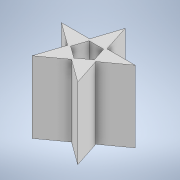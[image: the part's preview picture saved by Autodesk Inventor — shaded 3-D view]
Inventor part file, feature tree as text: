
AUTODESK INVENTOR PART (.ipt)
format: ipt  version: 2020.3 (Build 243373000, 373)  size: 107,008 bytes
history: native  units: mm
features: extrude x1, sketch x1
ambient origin geometry x8: Origin, YZ Plane, XZ Plane, XY Plane, X Axis, Y Axis, Z Axis, Center Point
bodies: Body1 (feature_tree)
feature tree (2):
  extrude  "Extrusion2"  Depth=32.0mm
  sketch  "Sketch1"  dims[d0=14.0mm d3=4.5mm d4=32.0mm d5=0.0mm d1=0.5mm d2=0.872665mm]
